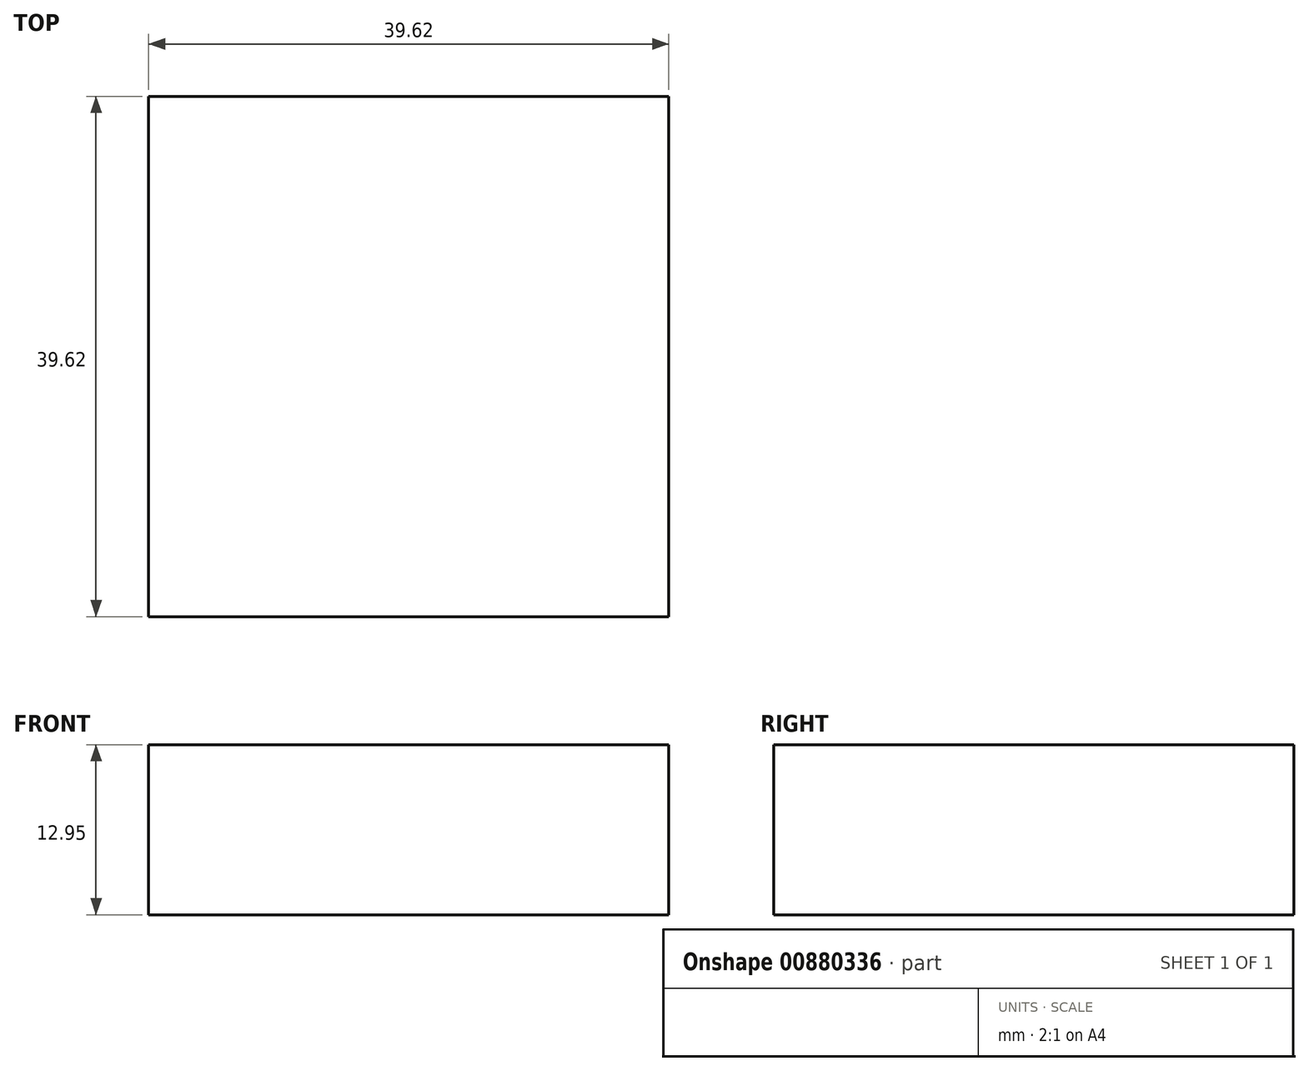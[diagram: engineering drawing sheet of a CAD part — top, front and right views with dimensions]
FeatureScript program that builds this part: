
annotation { "Feature Type Name" : "Feature", "Feature Type Description" : "" }
export const myFeature = defineFeature(function(context is Context, id is Id, definition is map)
    precondition{}
    {
        {
            var Q0;
            Q0=qCreatedBy(makeId("Top.planeOp"),FACE);
            var sketch = newSketch(context, id + "F0", { "sketchPlane" : qUnion([Q0])});
            skLineSegment(sketch, "E0.bottom", {"start": v(19.81, -19.81) * mm, "end": v(-19.81, -19.81) * mm});
            skLineSegment(sketch, "E0.top", {"start": v(19.81, 19.81) * mm, "end": v(-19.81, 19.81) * mm});
            skLineSegment(sketch, "E0.left", {"start": v(19.81, -19.81) * mm, "end": v(19.81, 19.81) * mm});
            skLineSegment(sketch, "E0.right", {"start": v(-19.81, -19.81) * mm, "end": v(-19.81, 19.81) * mm});
            skPoint(sketch, "E0.middle", {"position": v(0, 0) * mm});
            skSolve(sketch);
        }
        {
            var Q0;
            Q0=makeQuery(id+"F0.imprint","IMPRINT",FACE,{"disambiguationData":[TD([[makeQuery(id+"F0.imprint","IMPRINT",EDGE,{"derivedFrom":sQuery(id+"F0.wireOp",EDGE,"E0.bottom")}),-1.0]])]});
            extrude(context, id + "F1", {"entities" : qUnion([Q0]), "depth" : 12.95 * mm, "offsetDistance" : 25.4 * mm});
        }
    });
